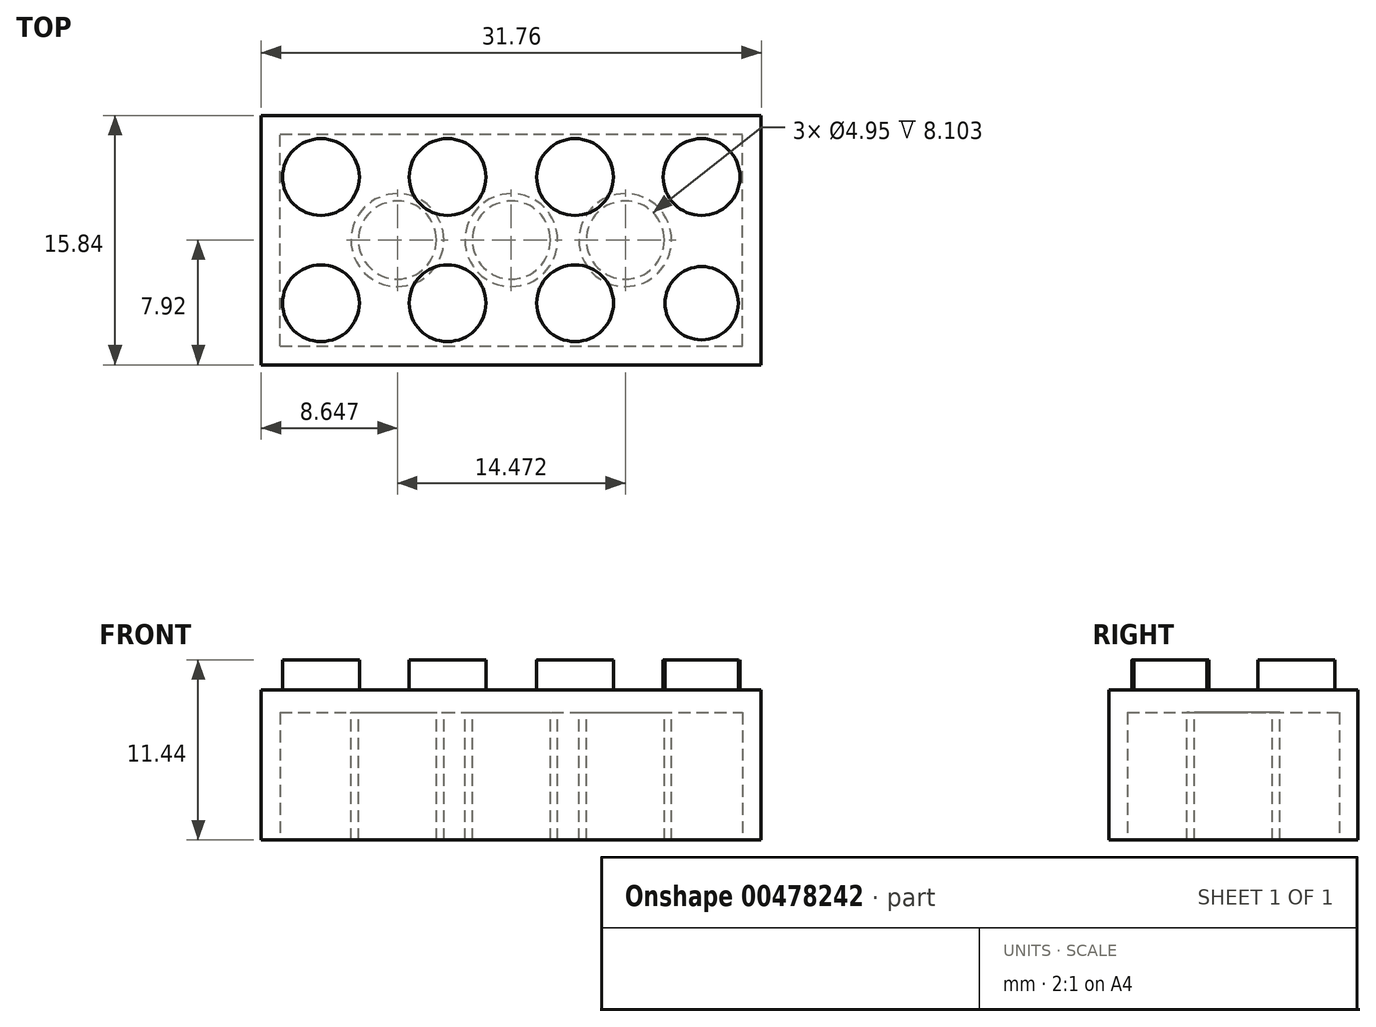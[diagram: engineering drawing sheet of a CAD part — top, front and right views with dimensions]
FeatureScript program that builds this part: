
annotation { "Feature Type Name" : "Feature", "Feature Type Description" : "" }
export const myFeature = defineFeature(function(context is Context, id is Id, definition is map)
    precondition{}
    {
        {
            var Q0;
            Q0=qCreatedBy(makeId("Top.planeOp"),FACE);
            var sketch = newSketch(context, id + "F0", { "sketchPlane" : qUnion([Q0])});
            skLineSegment(sketch, "E0.bottom", {"start": v(-15.87, 7.92) * mm, "end": v(15.88, 7.92) * mm});
            skLineSegment(sketch, "E0.top", {"start": v(-15.88, -7.92) * mm, "end": v(15.87, -7.92) * mm});
            skLineSegment(sketch, "E0.left", {"start": v(-15.88, 7.92) * mm, "end": v(-15.88, -7.92) * mm});
            skLineSegment(sketch, "E0.right", {"start": v(15.88, 7.92) * mm, "end": v(15.87, -7.92) * mm});
            skPoint(sketch, "E0.middle", {"position": v(0, 0) * mm});
            skSolve(sketch);
        }
        {
            var Q0;
            Q0 = qSketchRegion(id + "F0", true);
            extrude(context, id + "F1", {"entities" : qUnion([Q0]), "depth" : 9.55 * mm});
        }
        {
            var Q0;
            Q0=makeQuery(id+"F1.opExtrude","CAP_FACE",FACE,{"disambiguationData":[OSD([sQuery(id+"F0.wireOp",EDGE,"E0.bottom"),sQuery(id+"F0.wireOp",EDGE,"E0.top"),sQuery(id+"F0.wireOp",EDGE,"E0.left"),sQuery(id+"F0.wireOp",EDGE,"E0.right")])],"isStart":true});
            var sketch = newSketch(context, id + "F2", { "sketchPlane" : qUnion([Q0])});
            skLineSegment(sketch, "E1.bottom", {"start": v(-14.68, 6.72) * mm, "end": v(14.68, 6.72) * mm});
            skLineSegment(sketch, "E1.top", {"start": v(-14.68, -6.72) * mm, "end": v(14.68, -6.72) * mm});
            skLineSegment(sketch, "E1.left", {"start": v(-14.68, 6.72) * mm, "end": v(-14.68, -6.72) * mm});
            skLineSegment(sketch, "E1.right", {"start": v(14.68, 6.72) * mm, "end": v(14.68, -6.72) * mm});
            skPoint(sketch, "E1.middle", {"position": v(0, 0) * mm});
            skSolve(sketch);
        }
        {
            var Q0;
            Q0=makeQuery(id+"F2.imprint","IMPRINT",FACE,{"disambiguationData":[TD([[makeQuery(id+"F2.imprint","IMPRINT",EDGE,{"derivedFrom":sQuery(id+"F2.wireOp",EDGE,"E1.bottom")}),-1.0]])]});
            extrude(context, id + "F3", {"entities" : qUnion([Q0]), "operationType" : NewBodyOperationType.REMOVE, "oppositeDirection" : true, "depth" : 8.1 * mm});
        }
        {
            var Q0;
            Q0=makeQuery(id+"F1.opExtrude","CAP_FACE",FACE,{"disambiguationData":[OSD([sQuery(id+"F0.wireOp",EDGE,"E0.bottom"),sQuery(id+"F0.wireOp",EDGE,"E0.top"),sQuery(id+"F0.wireOp",EDGE,"E0.left"),sQuery(id+"F0.wireOp",EDGE,"E0.right")])],"isStart":false});
            var sketch = newSketch(context, id + "F4", { "sketchPlane" : qUnion([Q0])});
            skCircle(sketch, "E2", {"center": v(12.08, 4) * mm, "radius": 2.44 * mm});
            skCircle(sketch, "E3", {"center": v(4.04, 4) * mm, "radius": 2.44 * mm});
            skCircle(sketch, "E4", {"center": v(-4.05, 4) * mm, "radius": 2.44 * mm});
            skCircle(sketch, "E5", {"center": v(-12.1, 4) * mm, "radius": 2.44 * mm});
            skCircle(sketch, "E6", {"center": v(-12.1, -4) * mm, "radius": 2.44 * mm});
            skCircle(sketch, "E7", {"center": v(-4.05, -4) * mm, "radius": 2.44 * mm});
            skCircle(sketch, "E8", {"center": v(4.05, -4) * mm, "radius": 2.44 * mm});
            skCircle(sketch, "E9", {"center": v(12.1, -4) * mm, "radius": 2.33 * mm});
            skSolve(sketch);
        }
        {
            var Q0;
            Q0 = qSketchRegion(id + "F4", true);
            extrude(context, id + "F5", {"entities" : qUnion([Q0]), "operationType" : NewBodyOperationType.ADD, "depth" : 1.9 * mm});
        }
        {
            var Q0;
            Q0=makeQuery(id+"F3.boolean.opBoolean","COPY",FACE,{"derivedFrom":makeQuery(id+"F3.opExtrude","CAP_FACE",FACE,{"disambiguationData":[OSD([sQuery(id+"F2.wireOp",EDGE,"E1.bottom"),sQuery(id+"F2.wireOp",EDGE,"E1.top"),sQuery(id+"F2.wireOp",EDGE,"E1.left"),sQuery(id+"F2.wireOp",EDGE,"E1.right")])],"isStart":false})});
            var sketch = newSketch(context, id + "F6", { "sketchPlane" : qUnion([Q0])});
            skCircle(sketch, "E10", {"center": v(0, 0) * mm, "radius": 2.95 * mm});
            skCircle(sketch, "E11", {"center": v(-7.23, 0) * mm, "radius": 2.95 * mm});
            skCircle(sketch, "E12", {"center": v(7.24, 0) * mm, "radius": 2.48 * mm});
            skCircle(sketch, "E13", {"center": v(0, 0) * mm, "radius": 2.48 * mm});
            skCircle(sketch, "E14", {"center": v(-7.23, 0) * mm, "radius": 2.48 * mm});
            skCircle(sketch, "E15", {"center": v(7.24, 0) * mm, "radius": 2.95 * mm});
            skSolve(sketch);
        }
        {
            var Q0;
            Q0 = qSketchRegion(id + "F6", true);
            extrude(context, id + "F7", {"entities" : qUnion([Q0]), "operationType" : NewBodyOperationType.ADD, "depth" : 8.1 * mm});
        }
    });
